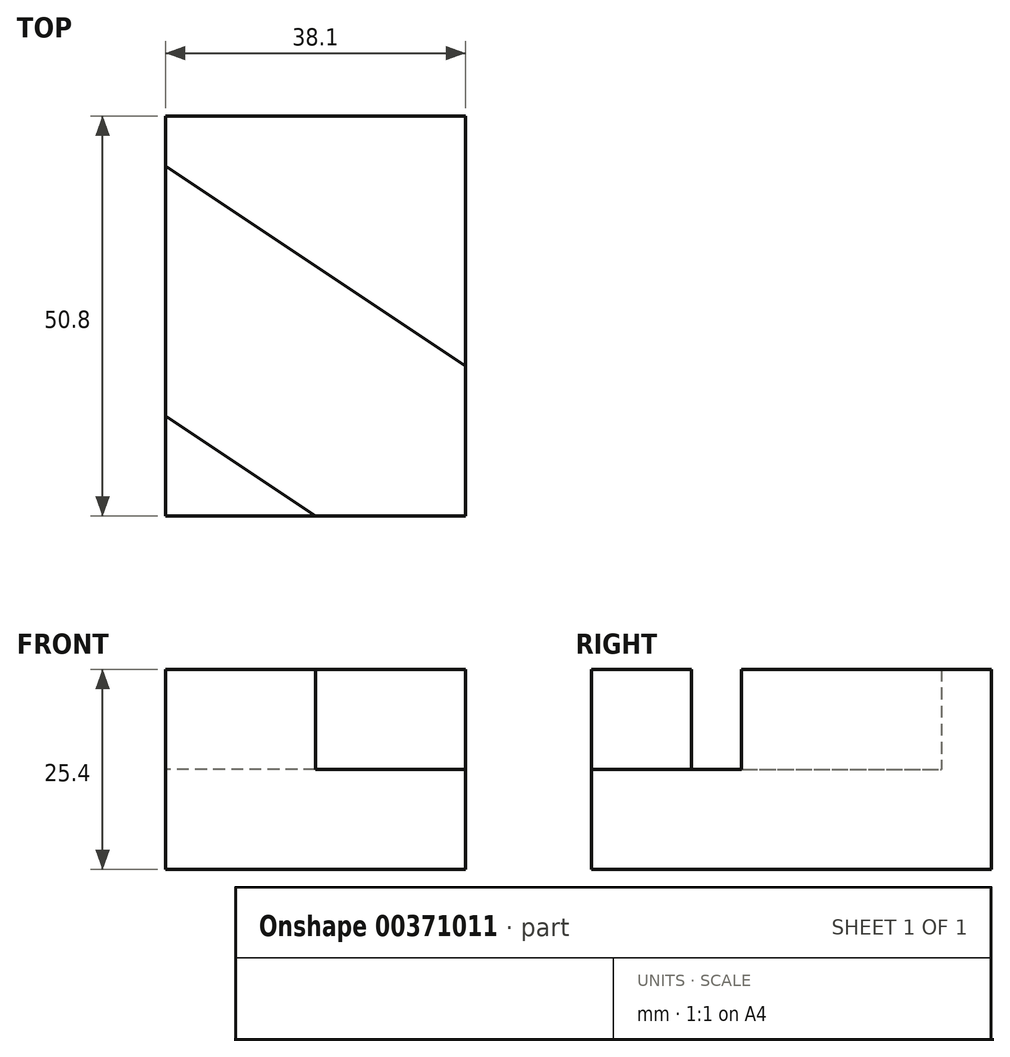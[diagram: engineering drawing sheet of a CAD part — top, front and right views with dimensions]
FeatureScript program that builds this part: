
annotation { "Feature Type Name" : "Feature", "Feature Type Description" : "" }
export const myFeature = defineFeature(function(context is Context, id is Id, definition is map)
    precondition{}
    {
        {
            var Q0;
            Q0=qCreatedBy(makeId("Top.planeOp"),FACE);
            var sketch = newSketch(context, id + "F0", { "sketchPlane" : qUnion([Q0])});
            skLineSegment(sketch, "E0", {"start": v(0, 0) * mm, "end": v(0, 50.8) * mm});
            skLineSegment(sketch, "E1", {"start": v(0, 50.8) * mm, "end": v(38.1, 50.8) * mm});
            skLineSegment(sketch, "E2", {"start": v(38.1, 50.8) * mm, "end": v(38.1, 0) * mm});
            skLineSegment(sketch, "E3", {"start": v(38.1, 0) * mm, "end": v(0, 0) * mm});
            skSolve(sketch);
        }
        {
            var Q0;
            Q0 = qSketchRegion(id + "F0", true);
            extrude(context, id + "F1", {"entities" : qUnion([Q0]), "oppositeDirection" : true, "depth" : 25.4 * mm});
        }
        {
            var Q0;
            Q0=makeQuery(id+"F1.opExtrude","CAP_FACE",FACE,{"disambiguationData":[OSD([sQuery(id+"F0.wireOp",EDGE,"E0"),sQuery(id+"F0.wireOp",EDGE,"E1"),sQuery(id+"F0.wireOp",EDGE,"E2"),sQuery(id+"F0.wireOp",EDGE,"E3")])],"isStart":true});
            var sketch = newSketch(context, id + "F2", { "sketchPlane" : qUnion([Q0])});
            skLineSegment(sketch, "E4", {"start": v(0, 0) * mm, "end": v(0, 12.7) * mm});
            skLineSegment(sketch, "E5", {"start": v(0, 12.7) * mm, "end": v(19.05, 0) * mm});
            skLineSegment(sketch, "E6", {"start": v(19.05, 0) * mm, "end": v(0, 0) * mm});
            skSolve(sketch);
        }
        {
            var Q0;
            Q0 = qSketchRegion(id + "F2", true);
            extrude(context, id + "F3", {"entities" : qUnion([Q0]), "operationType" : NewBodyOperationType.ADD, "depth" : 12.7 * mm});
        }
        {
            var Q0;
            Q0=makeQuery(id+"F1.opExtrude","CAP_FACE",FACE,{"disambiguationData":[OSD([sQuery(id+"F0.wireOp",EDGE,"E0"),sQuery(id+"F0.wireOp",EDGE,"E1"),sQuery(id+"F0.wireOp",EDGE,"E2"),sQuery(id+"F0.wireOp",EDGE,"E3")])],"isStart":true});
            var sketch = newSketch(context, id + "F4", { "sketchPlane" : qUnion([Q0])});
            skLineSegment(sketch, "E7", {"start": v(0, 50.8) * mm, "end": v(38.1, 50.8) * mm});
            skLineSegment(sketch, "E8", {"start": v(38.1, 50.8) * mm, "end": v(38.1, 19.05) * mm});
            skLineSegment(sketch, "E9", {"start": v(38.1, 19.05) * mm, "end": v(0, 44.45) * mm});
            skLineSegment(sketch, "E10", {"start": v(0, 44.45) * mm, "end": v(0, 50.8) * mm});
            skSolve(sketch);
        }
        {
            var Q0;
            Q0 = qSketchRegion(id + "F4", true);
            extrude(context, id + "F5", {"entities" : qUnion([Q0]), "operationType" : NewBodyOperationType.ADD, "depth" : 12.7 * mm});
        }
        {
            var Q0;
            Q0=makeQuery(id+"F5.boolean.opBoolean","MERGE",FACE,{"derivedFrom":[makeQuery(id+"F3.boolean.opBoolean","MERGE",FACE,{"derivedFrom":[makeQuery(id+"F1.opExtrude","SWEPT_FACE",FACE,{"disambiguationData":[OSD([sQuery(id+"F0.wireOp",EDGE,"E0")])]}),makeQuery(id+"F3.opExtrude","SWEPT_FACE",FACE,{"disambiguationData":[OSD([sQuery(id+"F2.wireOp",EDGE,"E4")])]})]}),makeQuery(id+"F5.opExtrude","SWEPT_FACE",FACE,{"disambiguationData":[OSD([sQuery(id+"F4.wireOp",EDGE,"E10")])]})]});
            var sketch = newSketch(context, id + "F6", { "sketchPlane" : qUnion([Q0])});
            skLineSegment(sketch, "E11", {"start": v(-50.8, -25.4) * mm, "end": v(-50.8, -12.7) * mm});
            skLineSegment(sketch, "E12", {"start": v(-50.8, -12.7) * mm, "end": v(0, -12.7) * mm});
            skLineSegment(sketch, "E13", {"start": v(0, -12.7) * mm, "end": v(0, -25.4) * mm});
            skLineSegment(sketch, "E14", {"start": v(0, -25.4) * mm, "end": v(-50.8, -25.4) * mm});
            skSolve(sketch);
        }
        {
            var Q0;
            Q0 = qSketchRegion(id + "F6", true);
            extrude(context, id + "F7", {"entities" : qUnion([Q0]), "operationType" : NewBodyOperationType.REMOVE, "oppositeDirection" : true, "depth" : 38.1 * mm});
        }
    });
